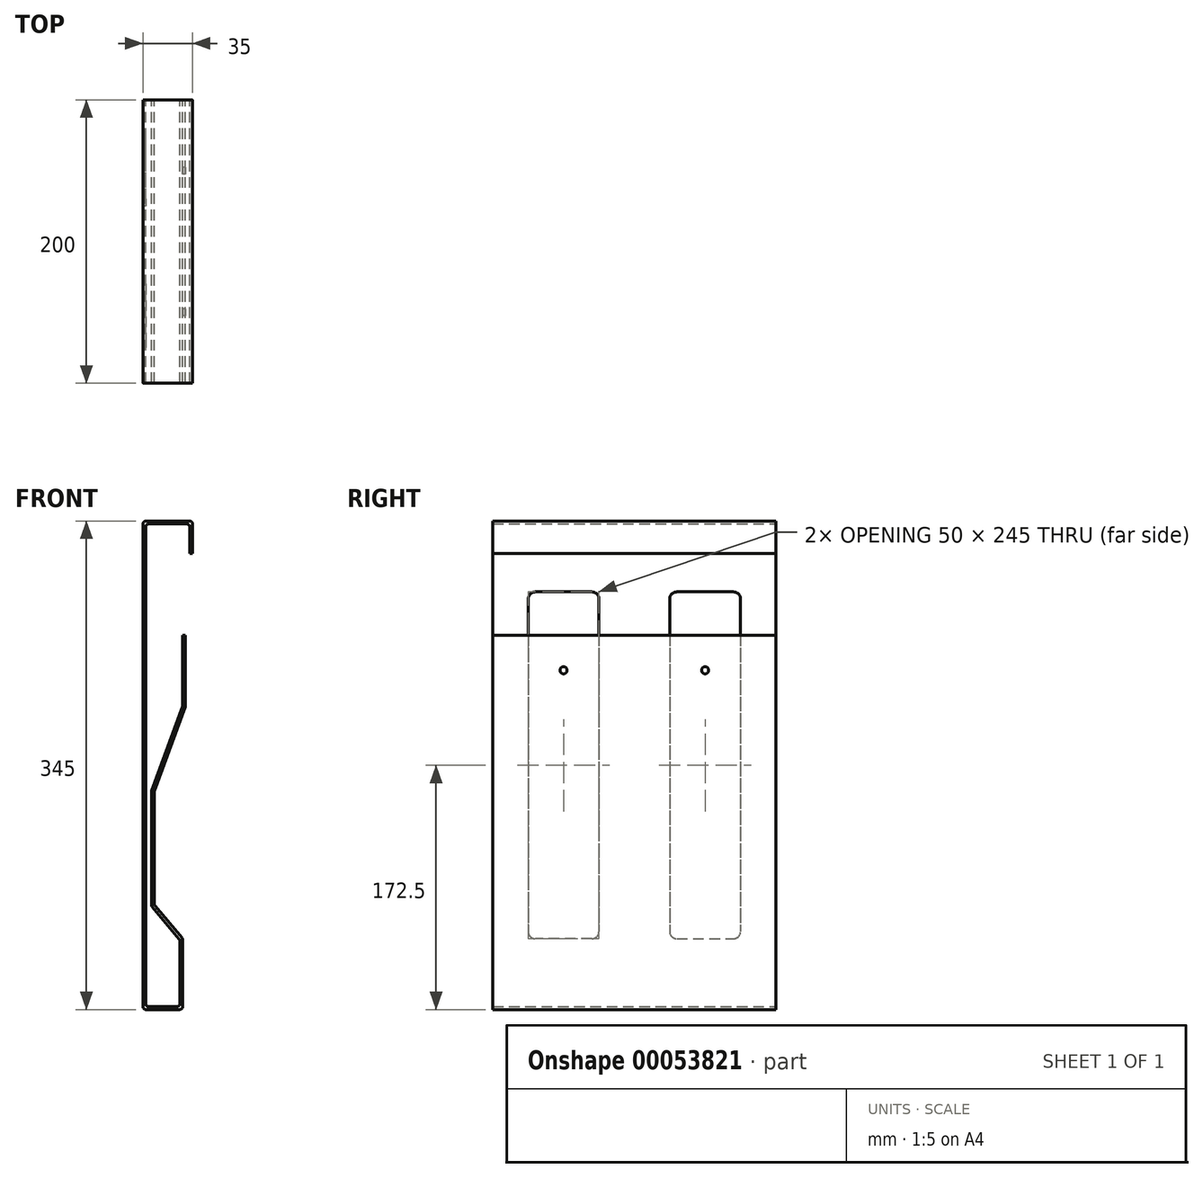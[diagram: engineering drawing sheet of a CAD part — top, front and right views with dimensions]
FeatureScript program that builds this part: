
annotation { "Feature Type Name" : "Feature", "Feature Type Description" : "" }
export const myFeature = defineFeature(function(context is Context, id is Id, definition is map)
    precondition{}
    {
        {
            var Q0;
            Q0=qCreatedBy(makeId("Front.planeOp"),FACE);
            var sketch = newSketch(context, id + "F0", { "sketchPlane" : qUnion([Q0])});
            skLineSegment(sketch, "E0", {"start": v(0, 0) * mm, "end": v(35, 0) * mm});
            skLineSegment(sketch, "E1", {"start": v(35, 0) * mm, "end": v(35, -23) * mm});
            skLineSegment(sketch, "E2", {"start": v(0, 0) * mm, "end": v(0, -345) * mm});
            skLineSegment(sketch, "E3", {"start": v(0, -345) * mm, "end": v(28, -345) * mm});
            skLineSegment(sketch, "E4", {"start": v(28, -295) * mm, "end": v(28, -345) * mm});
            skLineSegment(sketch, "E5.0", {"start": v(33, -2) * mm, "end": v(33, -23) * mm});
            skLineSegment(sketch, "E5.1", {"start": v(26, -295.73) * mm, "end": v(26, -343) * mm});
            skLineSegment(sketch, "E5.2", {"start": v(2, -343) * mm, "end": v(26, -343) * mm});
            skLineSegment(sketch, "E5.3", {"start": v(2, -2) * mm, "end": v(2, -343) * mm});
            skLineSegment(sketch, "E5.4", {"start": v(2, -2) * mm, "end": v(33, -2) * mm});
            skLineSegment(sketch, "E6", {"start": v(33, -23) * mm, "end": v(35, -23) * mm});
            skLineSegment(sketch, "E7", {"start": v(26, -295.73) * mm, "end": v(6, -271.9) * mm});
            skLineSegment(sketch, "E8", {"start": v(6, -271.9) * mm, "end": v(6, -190.81) * mm});
            skLineSegment(sketch, "E9", {"start": v(6, -190.81) * mm, "end": v(28, -130.37) * mm});
            skLineSegment(sketch, "E10", {"start": v(28, -130.37) * mm, "end": v(28, -80.72) * mm});
            skLineSegment(sketch, "E11.0", {"start": v(30, -130.72) * mm, "end": v(30, -80.72) * mm});
            skLineSegment(sketch, "E11.1", {"start": v(8, -191.16) * mm, "end": v(30, -130.72) * mm});
            skLineSegment(sketch, "E11.2", {"start": v(8, -271.16) * mm, "end": v(8, -191.16) * mm});
            skLineSegment(sketch, "E11.3", {"start": v(28, -295) * mm, "end": v(8, -271.16) * mm});
            skLineSegment(sketch, "E12", {"start": v(28, -80.72) * mm, "end": v(30, -80.72) * mm});
            skSolve(sketch);
        }
        {
            var Q0;
            Q0=qSketchRegion(id+"F0",true);
            extrude(context, id + "F1", {"entities" : qUnion([Q0]), "depth" : 200 * mm});
        }
        {
            var Q0;
            Q0=makeQuery(id+"F1.opExtrude","SWEPT_EDGE",EDGE,{"disambiguationData":[OSD([sQuery(id+"F0.wireOp",EDGE,"E0"),sQuery(id+"F0.wireOp",EDGE,"E2")])]});
            var Q1;
            Q1=makeQuery(id+"F1.opExtrude","SWEPT_EDGE",EDGE,{"disambiguationData":[OSD([sQuery(id+"F0.wireOp",EDGE,"E0"),sQuery(id+"F0.wireOp",EDGE,"E1")])]});
            var Q2;
            Q2=makeQuery(id+"F1.opExtrude","SWEPT_EDGE",EDGE,{"disambiguationData":[OSD([sQuery(id+"F0.wireOp",EDGE,"E5.0"),sQuery(id+"F0.wireOp",EDGE,"E5.4")])]});
            var Q3;
            Q3=makeQuery(id+"F1.opExtrude","SWEPT_EDGE",EDGE,{"disambiguationData":[OSD([sQuery(id+"F0.wireOp",EDGE,"E5.3"),sQuery(id+"F0.wireOp",EDGE,"E5.4")])]});
            var Q4;
            Q4=makeQuery(id+"F1.opExtrude","SWEPT_EDGE",EDGE,{"disambiguationData":[OSD([sQuery(id+"F0.wireOp",EDGE,"E2"),sQuery(id+"F0.wireOp",EDGE,"E3")])]});
            var Q5;
            Q5=makeQuery(id+"F1.opExtrude","SWEPT_EDGE",EDGE,{"disambiguationData":[OSD([sQuery(id+"F0.wireOp",EDGE,"E5.2"),sQuery(id+"F0.wireOp",EDGE,"E5.3")])]});
            var Q6;
            Q6=makeQuery(id+"F1.opExtrude","SWEPT_EDGE",EDGE,{"disambiguationData":[OSD([sQuery(id+"F0.wireOp",EDGE,"E3"),sQuery(id+"F0.wireOp",EDGE,"E4")])]});
            var Q7;
            Q7=makeQuery(id+"F1.opExtrude","SWEPT_EDGE",EDGE,{"disambiguationData":[OSD([sQuery(id+"F0.wireOp",EDGE,"E5.1"),sQuery(id+"F0.wireOp",EDGE,"E5.2")])]});
            var Q8;
            Q8=makeQuery(id+"F1.opExtrude","SWEPT_EDGE",EDGE,{"disambiguationData":[OSD([sQuery(id+"F0.wireOp",EDGE,"E5.1"),sQuery(id+"F0.wireOp",EDGE,"E7")])]});
            var Q9;
            Q9=makeQuery(id+"F1.opExtrude","SWEPT_EDGE",EDGE,{"disambiguationData":[OSD([sQuery(id+"F0.wireOp",EDGE,"E4"),sQuery(id+"F0.wireOp",EDGE,"E11.3")])]});
            var Q10;
            Q10=makeQuery(id+"F1.opExtrude","SWEPT_EDGE",EDGE,{"disambiguationData":[OSD([sQuery(id+"F0.wireOp",EDGE,"E11.2"),sQuery(id+"F0.wireOp",EDGE,"E11.3")])]});
            var Q11;
            Q11=makeQuery(id+"F1.opExtrude","SWEPT_EDGE",EDGE,{"disambiguationData":[OSD([sQuery(id+"F0.wireOp",EDGE,"E7"),sQuery(id+"F0.wireOp",EDGE,"E8")])]});
            var Q12;
            Q12=makeQuery(id+"F1.opExtrude","SWEPT_EDGE",EDGE,{"disambiguationData":[OSD([sQuery(id+"F0.wireOp",EDGE,"E8"),sQuery(id+"F0.wireOp",EDGE,"E9")])]});
            var Q13;
            Q13=makeQuery(id+"F1.opExtrude","SWEPT_EDGE",EDGE,{"disambiguationData":[OSD([sQuery(id+"F0.wireOp",EDGE,"E11.1"),sQuery(id+"F0.wireOp",EDGE,"E11.2")])]});
            var Q14;
            Q14=makeQuery(id+"F1.opExtrude","SWEPT_EDGE",EDGE,{"disambiguationData":[OSD([sQuery(id+"F0.wireOp",EDGE,"E11.0"),sQuery(id+"F0.wireOp",EDGE,"E11.1")])]});
            var Q15;
            Q15=makeQuery(id+"F1.opExtrude","SWEPT_EDGE",EDGE,{"disambiguationData":[OSD([sQuery(id+"F0.wireOp",EDGE,"E9"),sQuery(id+"F0.wireOp",EDGE,"E10")])]});
            fillet(context, id + "F2", {"entities" : qUnion([Q0, Q1, Q2, Q3, Q4, Q5, Q6, Q7, Q8, Q9, Q10, Q11, Q12, Q13, Q14, Q15]), "radius" : 2 * mm, "tangentPropagation" : true, "allowEdgeOverflow" : false});
        }
        {
            var Q0;
            Q0=makeQuery(id+"F1.opExtrude","SWEPT_FACE",FACE,{"disambiguationData":[OSD([sQuery(id+"F0.wireOp",EDGE,"E2")])]});
            var sketch = newSketch(context, id + "F3", { "sketchPlane" : qUnion([Q0])});
            skLineSegment(sketch, "E13", {"start": v(100, -2) * mm, "end": v(100, -30.26) * mm, "construction": true});
            skPoint(sketch, "E13.endSnap0", {"position": v(100, -2) * mm});
            skLineSegment(sketch, "E14.bottom", {"start": v(70, -50) * mm, "end": v(30, -50) * mm});
            skLineSegment(sketch, "E14.top", {"start": v(70, -295) * mm, "end": v(30, -295) * mm});
            skLineSegment(sketch, "E14.left", {"start": v(75, -55) * mm, "end": v(75, -290) * mm});
            skLineSegment(sketch, "E14.right", {"start": v(25, -55) * mm, "end": v(25, -290) * mm});
            skPoint(sketch, "E15.visualSharp", {"position": v(25, -50) * mm});
            skArc(sketch, "E15.filletArc", {"start": v(30, -50) * mm, "mid": v(26.46, -51.46) * mm, "end": v(25, -55) * mm});
            skPoint(sketch, "E16.visualSharp", {"position": v(75, -50) * mm});
            skArc(sketch, "E16.filletArc", {"start": v(75, -55) * mm, "mid": v(73.54, -51.46) * mm, "end": v(70, -50) * mm});
            skPoint(sketch, "E17.visualSharp", {"position": v(75, -295) * mm});
            skArc(sketch, "E17.filletArc", {"start": v(70, -295) * mm, "mid": v(73.54, -293.54) * mm, "end": v(75, -290) * mm});
            skPoint(sketch, "E18.visualSharp", {"position": v(25, -295) * mm});
            skArc(sketch, "E18.filletArc", {"start": v(25, -290) * mm, "mid": v(26.46, -293.54) * mm, "end": v(30, -295) * mm});
            skArc(sketch, "E19.MirrorCS", {"start": v(175, -290) * mm, "mid": v(173.54, -293.54) * mm, "end": v(170, -295) * mm});
            skArc(sketch, "E20.MirrorCS", {"start": v(130, -295) * mm, "mid": v(126.46, -293.54) * mm, "end": v(125, -290) * mm});
            skArc(sketch, "E21.MirrorCS", {"start": v(125, -55) * mm, "mid": v(126.46, -51.46) * mm, "end": v(130, -50) * mm});
            skArc(sketch, "E22.MirrorCS", {"start": v(170, -50) * mm, "mid": v(173.54, -51.46) * mm, "end": v(175, -55) * mm});
            skPoint(sketch, "E23.MirrorP", {"position": v(125, -295) * mm});
            skPoint(sketch, "E24.MirrorP", {"position": v(175, -295) * mm});
            skLineSegment(sketch, "E25.MirrorCS", {"start": v(130, -50) * mm, "end": v(170, -50) * mm});
            skLineSegment(sketch, "E26.MirrorCS", {"start": v(130, -295) * mm, "end": v(170, -295) * mm});
            skPoint(sketch, "E27.MirrorP", {"position": v(125, -50) * mm});
            skLineSegment(sketch, "E28.MirrorCS", {"start": v(125, -55) * mm, "end": v(125, -290) * mm});
            skPoint(sketch, "E29.MirrorP", {"position": v(175, -50) * mm});
            skLineSegment(sketch, "E30.MirrorCS", {"start": v(175, -55) * mm, "end": v(175, -290) * mm});
            skSolve(sketch);
        }
        {
            var Q0;
            Q0 = qSketchRegion(id + "F3", true);
            extrude(context, id + "F4", {"entities" : qUnion([Q0]), "operationType" : NewBodyOperationType.REMOVE, "oppositeDirection" : true, "depth" : 2 * mm});
        }
        {
            var Q0;
            Q0=makeQuery(id+"F1.opExtrude","SWEPT_FACE",FACE,{"disambiguationData":[OSD([sQuery(id+"F0.wireOp",EDGE,"E10")])]});
            var sketch = newSketch(context, id + "F5", { "sketchPlane" : qUnion([Q0])});
            skLineSegment(sketch, "E31", {"start": v(0, -105.37) * mm, "end": v(200, -105.37) * mm, "construction": true});
            skPoint(sketch, "E32", {"position": v(50, -105.37) * mm});
            skPoint(sketch, "E33", {"position": v(150, -105.37) * mm});
            skSolve(sketch);
        }
        {
            var Q0;
            Q0=sQuery(id+"F5.wireOp",VERTEX,"E32");
            var Q1;
            Q1=sQuery(id+"F5.wireOp",VERTEX,"E33");
            var Q2;
            Q2=makeQuery(id+"F1.opExtrude","SWEPT_BODY",BODY,{"disambiguationData":[OSD([sQuery(id+"F0.wireOp",EDGE,"E0"),sQuery(id+"F0.wireOp",EDGE,"E1"),sQuery(id+"F0.wireOp",EDGE,"E2"),sQuery(id+"F0.wireOp",EDGE,"E3"),sQuery(id+"F0.wireOp",EDGE,"E4"),sQuery(id+"F0.wireOp",EDGE,"E5.0"),sQuery(id+"F0.wireOp",EDGE,"E5.1"),sQuery(id+"F0.wireOp",EDGE,"E5.2"),sQuery(id+"F0.wireOp",EDGE,"E5.3"),sQuery(id+"F0.wireOp",EDGE,"E5.4"),sQuery(id+"F0.wireOp",EDGE,"E6"),sQuery(id+"F0.wireOp",EDGE,"E7"),sQuery(id+"F0.wireOp",EDGE,"E8"),sQuery(id+"F0.wireOp",EDGE,"E9"),sQuery(id+"F0.wireOp",EDGE,"E10"),sQuery(id+"F0.wireOp",EDGE,"E11.0"),sQuery(id+"F0.wireOp",EDGE,"E11.1"),sQuery(id+"F0.wireOp",EDGE,"E11.2"),sQuery(id+"F0.wireOp",EDGE,"E11.3"),sQuery(id+"F0.wireOp",EDGE,"E12")])]});
            hole(context, id + "F6", {"style" : HoleStyle.SIMPLE, "endStyle" : HoleEndStyle.BLIND, "holeDiameter" : 5 * mm, "holeDepth" : 2 * mm, "locations" : qUnion([Q0, Q1]), "scope" : qUnion([Q2])});
        }
    });
